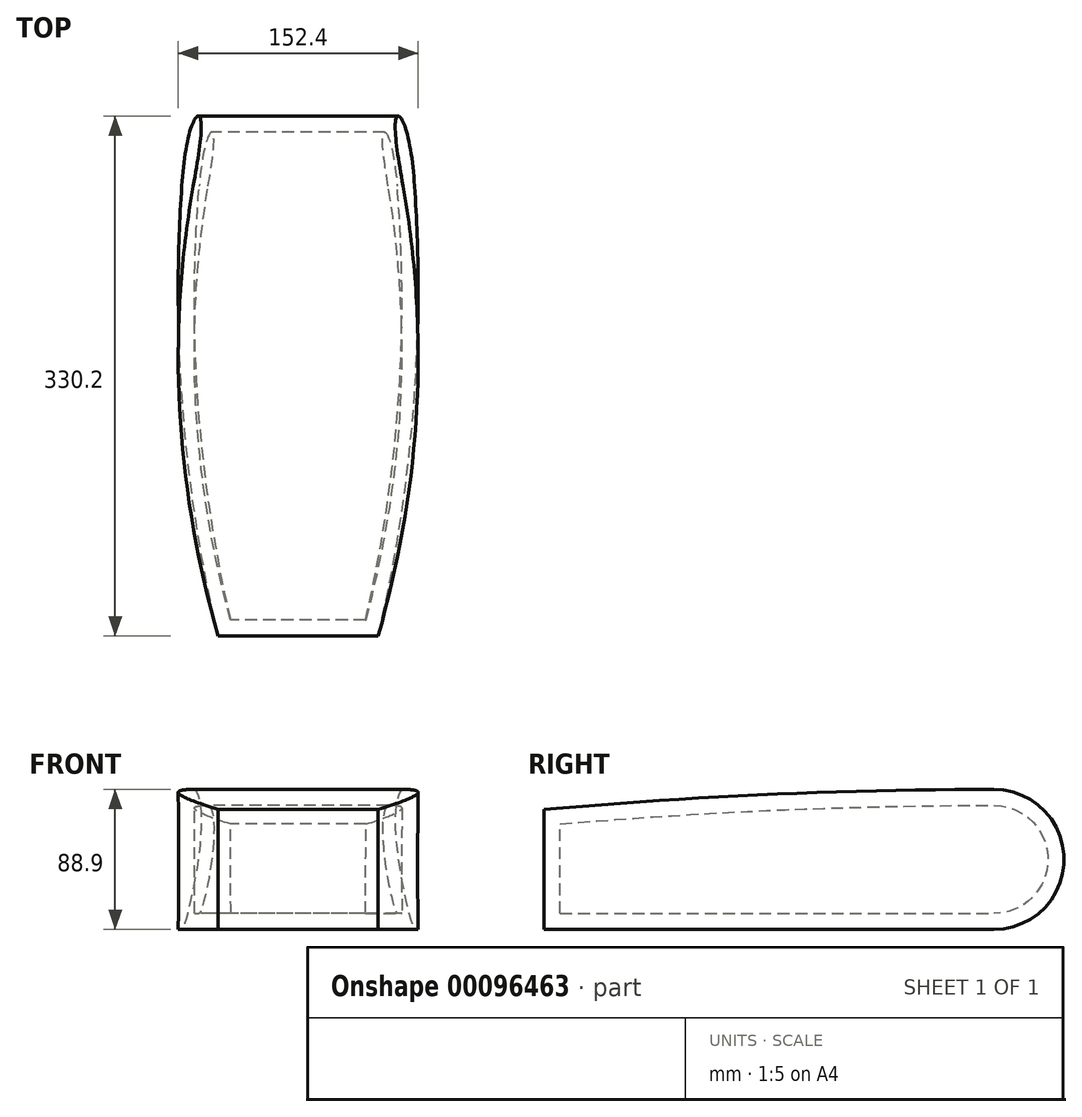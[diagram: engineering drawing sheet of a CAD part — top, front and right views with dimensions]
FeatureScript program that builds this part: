
annotation { "Feature Type Name" : "Feature", "Feature Type Description" : "" }
export const myFeature = defineFeature(function(context is Context, id is Id, definition is map)
    precondition{}
    {
        {
            var Q0;
            Q0=qCreatedBy(makeId("Right.planeOp"),FACE);
            var sketch = newSketch(context, id + "F0", { "sketchPlane" : qUnion([Q0])});
            skLineSegment(sketch, "E0.bottom", {"start": v(-254, 38.1) * mm, "end": v(76.2, 38.1) * mm});
            skLineSegment(sketch, "E0.top", {"start": v(-254, -50.8) * mm, "end": v(76.2, -50.8) * mm});
            skLineSegment(sketch, "E0.left", {"start": v(-254, 38.1) * mm, "end": v(-254, -50.8) * mm});
            skLineSegment(sketch, "E0.right", {"start": v(76.2, 38.1) * mm, "end": v(76.2, -50.8) * mm});
            skSolve(sketch);
        }
        {
            var Q0;
            Q0=qCreatedBy(makeId("Top.planeOp"),FACE);
            var sketch = newSketch(context, id + "F1", { "sketchPlane" : qUnion([Q0])});
            skLineSegment(sketch, "E1.bottom", {"start": v(0, 76.2) * mm, "end": v(76.2, 76.2) * mm});
            skLineSegment(sketch, "E1.top", {"start": v(0, -254) * mm, "end": v(76.2, -254) * mm});
            skLineSegment(sketch, "E1.left", {"start": v(0, 76.2) * mm, "end": v(0, -254) * mm});
            skLineSegment(sketch, "E1.right", {"start": v(76.2, 76.2) * mm, "end": v(76.2, -254) * mm});
            skSolve(sketch);
        }
        {
            var Q0;
            Q0=qCreatedBy(makeId("Front.planeOp"),FACE);
            var sketch = newSketch(context, id + "F2", { "sketchPlane" : qUnion([Q0])});
            skLineSegment(sketch, "E2.bottom", {"start": v(0, 38.1) * mm, "end": v(76.2, 38.1) * mm});
            skLineSegment(sketch, "E2.top", {"start": v(0, -50.8) * mm, "end": v(76.2, -50.8) * mm});
            skLineSegment(sketch, "E2.left", {"start": v(0, 38.1) * mm, "end": v(0, -50.8) * mm});
            skLineSegment(sketch, "E2.right", {"start": v(76.2, 38.1) * mm, "end": v(76.2, -50.8) * mm});
            skSolve(sketch);
        }
        {
            var Q0;
            Q0=sQuery(id+"F0.wireOp",VERTEX,"E0.bottom.start");
            var Q1;
            Q1=sQuery(id+"F0.wireOp",VERTEX,"E0.right.start");
            var Q2;
            Q2=sQuery(id+"F2.wireOp",VERTEX,"E2.right.start");
            cPlane(context, id + "F3", {"entities" : qUnion([Q0, Q1, Q2]), "cplaneType" : CPlaneType.THREE_POINT, "offset" : 152.4 * mm, "width" : 152.4 * mm, "height" : 152.4 * mm});
        }
        {
            var Q0;
            Q0=sQuery(id+"F0.wireOp",VERTEX,"E0.top.start");
            var Q1;
            Q1=sQuery(id+"F2.wireOp",VERTEX,"E2.top.end");
            var Q2;
            Q2=sQuery(id+"F0.wireOp",VERTEX,"E0.top.end");
            cPlane(context, id + "F4", {"entities" : qUnion([Q0, Q1, Q2]), "cplaneType" : CPlaneType.THREE_POINT, "offset" : 152.4 * mm, "width" : 152.4 * mm, "height" : 152.4 * mm});
        }
        {
            var Q0;
            Q0=qCreatedBy(id+"F4.planeOp",FACE);
            var sketch = newSketch(context, id + "F5", { "sketchPlane" : qUnion([Q0])});
            skArc(sketch, "E3", {"start": v(69.85, -76.2) * mm, "mid": v(74.6, 89.72) * mm, "end": v(50.8, 254) * mm});
            skSolve(sketch);
        }
        {
            var Q0;
            Q0=qCreatedBy(id+"F3.planeOp",FACE);
            var sketch = newSketch(context, id + "F6", { "sketchPlane" : qUnion([Q0])});
            skArc(sketch, "E4", {"start": v(50.8, -254) * mm, "mid": v(76.08, -89.33) * mm, "end": v(57.15, 76.2) * mm});
            skSolve(sketch);
        }
        {
            var Q0;
            Q0=sQuery(id+"F6.wireOp",EDGE,"E4");
            extrude(context, id + "F7", {"bodyType" : ToolBodyType.SURFACE, "surfaceEntities" : qUnion([Q0]), "depth" : 25.4 * mm});
        }
        {
            var Q0;
            Q0=makeQuery(id+"F7.opExtrude","SWEPT_BODY",BODY,{"disambiguationData":[OSD([sQuery(id+"F5.wireOp",EDGE,"E3")])]});
            var Q1;
            Q1=sQuery(id+"F6.wireOp",EDGE,"E4");
            var Q2;
            Q2=sQuery(id+"F5.wireOp",EDGE,"E3");
            loft(context, id + "F8", {"bodyType" : ToolBodyType.SURFACE, "sheetProfilesArray" : [{ "sheetProfileEntities" : qUnion([Q0]) }], "wireProfilesArray" : [{ "wireProfileEntities" : qUnion([Q1]) }, { "wireProfileEntities" : qUnion([Q2]) }]});
        }
        {
            var Q0;
            Q0=qCreatedBy(makeId("Right.planeOp"),FACE);
            var sketch = newSketch(context, id + "F9", { "sketchPlane" : qUnion([Q0])});
            skArc(sketch, "E5", {"start": v(31.75, 38.1) * mm, "mid": v(-111.27, 34.92) * mm, "end": v(-254, 25.4) * mm});
            skArc(sketch, "E6", {"start": v(31.75, -50.8) * mm, "mid": v(76.2, -6.35) * mm, "end": v(31.75, 38.1) * mm});
            skPoint(sketch, "E6.first.point", {"position": v(31.75, -50.8) * mm});
            skPoint(sketch, "E6.second.point", {"position": v(31.75, 38.1) * mm});
            skPoint(sketch, "E6.third.point", {"position": v(76.2, -6.35) * mm});
            skLineSegment(sketch, "E7", {"start": v(31.75, -50.8) * mm, "end": v(-254, -50.8) * mm});
            skLineSegment(sketch, "E8", {"start": v(-254, 25.4) * mm, "end": v(-254, -50.8) * mm});
            skSolve(sketch);
        }
        {
            var Q0;
            Q0 = qSketchRegion(id + "F9", true);
            var Q1;
            Q1=makeQuery(id+"F8.opLoft","SWEPT_FACE",FACE,{"disambiguationData":[OSD([sQuery(id+"F5.wireOp",VERTEX,"E3.start"),sQuery(id+"F5.wireOp",VERTEX,"E3.end"),sQuery(id+"F5.wireOp",EDGE,"E3"),sQuery(id+"F6.wireOp",VERTEX,"E4.start"),sQuery(id+"F6.wireOp",VERTEX,"E4.end"),sQuery(id+"F6.wireOp",EDGE,"E4")])]});
            extrude(context, id + "F10", {"entities" : qUnion([Q0]), "endBound" : BoundingType.UP_TO_SURFACE, "endBoundEntityFace" : qUnion([Q1]), "depth" : 25.4 * mm});
        }
        {
            var Q0;
            Q0=makeQuery(id+"F10.opExtrude","CAP_FACE",FACE,{"disambiguationData":[OSD([sQuery(id+"F9.wireOp",EDGE,"E5"),sQuery(id+"F9.wireOp",EDGE,"E6"),sQuery(id+"F9.wireOp",EDGE,"E7"),sQuery(id+"F9.wireOp",EDGE,"E8")])],"isStart":true});
            shell(context, id + "F11", {"entities" : qUnion([Q0]), "thickness" : 10.16 * mm});
        }
        {
            var Q0;
            Q0=makeQuery(id+"F10.opExtrude","SWEPT_BODY",BODY,{"disambiguationData":[OSD([sQuery(id+"F9.wireOp",EDGE,"E5"),sQuery(id+"F9.wireOp",EDGE,"E6"),sQuery(id+"F9.wireOp",EDGE,"E7"),sQuery(id+"F9.wireOp",EDGE,"E8")])]});
            var Q1;
            Q1=qCreatedBy(makeId("Right.planeOp"),FACE);
            mirror(context, id + "F12", {"operationType" : NewBodyOperationType.ADD, "entities" : qUnion([Q0]), "mirrorPlane" : qUnion([Q1])});
        }
    });
